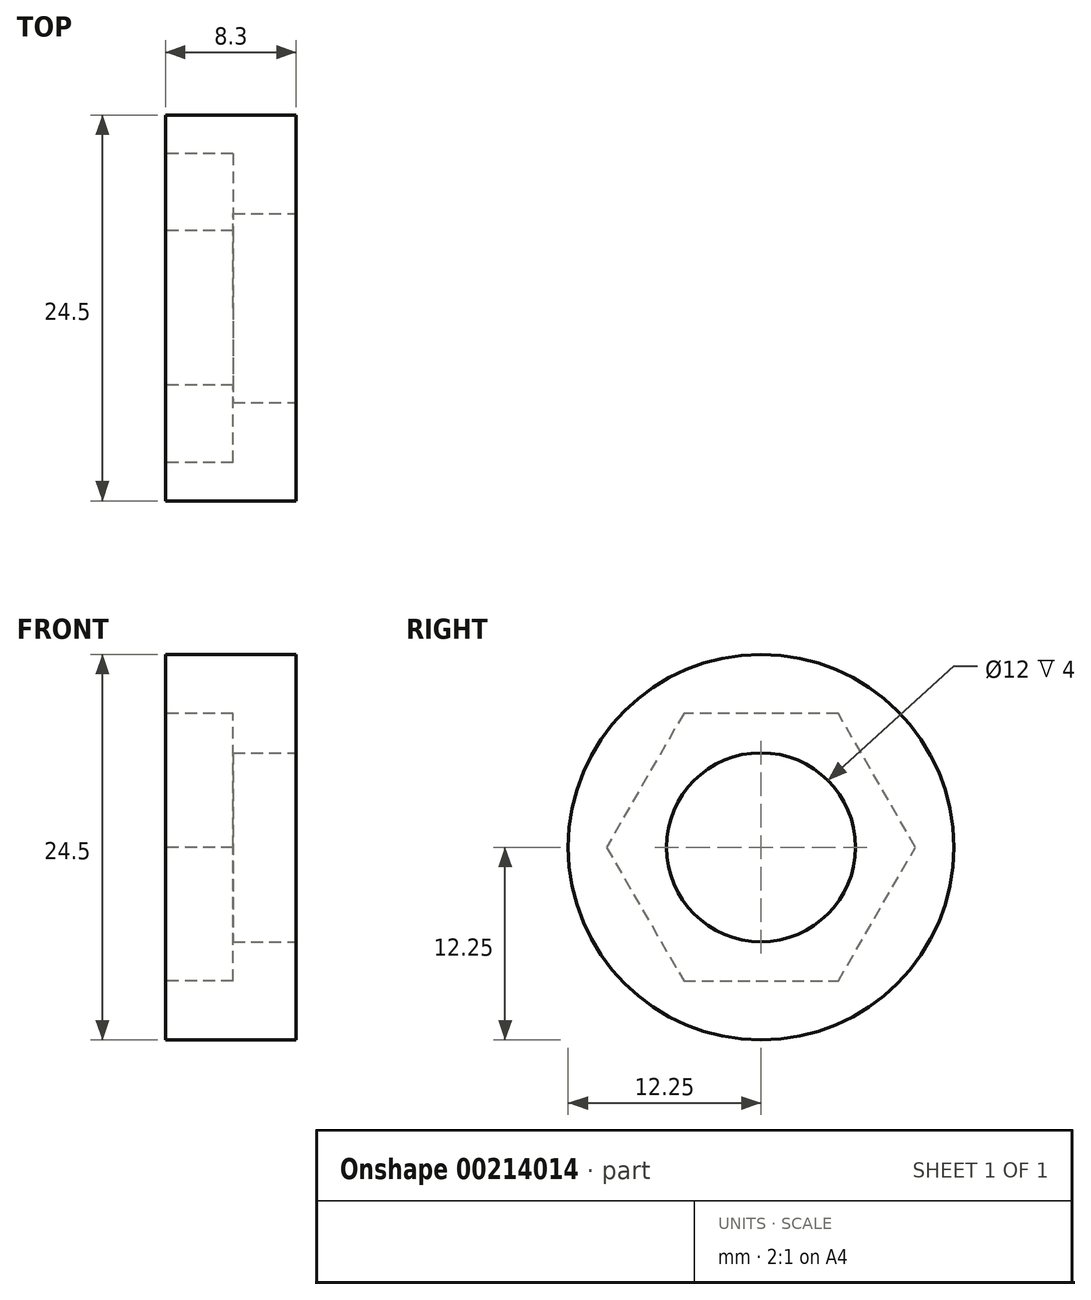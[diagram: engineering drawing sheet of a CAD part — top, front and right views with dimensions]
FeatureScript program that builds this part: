
annotation { "Feature Type Name" : "Feature", "Feature Type Description" : "" }
export const myFeature = defineFeature(function(context is Context, id is Id, definition is map)
    precondition{}
    {
        {
            var Q0;
            Q0=qCreatedBy(makeId("Right.planeOp"),FACE);
            var sketch = newSketch(context, id + "F0", { "sketchPlane" : qUnion([Q0])});
            skCircle(sketch, "E0", {"center": v(0, 0) * mm, "radius": 12.25 * mm});
            skSolve(sketch);
        }
        {
            var Q0;
            Q0 = qSketchRegion(id + "F0", true);
            extrude(context, id + "F1", {"entities" : qUnion([Q0]), "depth" : 8.3 * mm});
        }
        {
            var Q0;
            Q0=makeQuery(id+"F1.opExtrude","CAP_FACE",FACE,{"disambiguationData":[OSD([sQuery(id+"F0.wireOp",EDGE,"E0")])],"isStart":false});
            var sketch = newSketch(context, id + "F2", { "sketchPlane" : qUnion([Q0])});
            skCircle(sketch, "E1", {"center": v(0, 0) * mm, "radius": 6 * mm});
            skSolve(sketch);
        }
        {
            var Q0;
            Q0 = qSketchRegion(id + "F2", true);
            extrude(context, id + "F3", {"entities" : qUnion([Q0]), "operationType" : NewBodyOperationType.REMOVE, "endBound" : BoundingType.THROUGH_ALL, "oppositeDirection" : true, "depth" : 25.4 * mm});
        }
        {
            var Q0;
            Q0=makeQuery(id+"F1.opExtrude","CAP_FACE",FACE,{"disambiguationData":[OSD([sQuery(id+"F0.wireOp",EDGE,"E0")])],"isStart":true});
            var sketch = newSketch(context, id + "F4", { "sketchPlane" : qUnion([Q0])});
            skCircle(sketch, "E2.cCircle", {"center": v(0, 0) * mm, "radius": 8.5 * mm, "construction": true});
            skLineSegment(sketch, "E2.0", {"start": v(-4.9, 8.5) * mm, "end": v(4.9, 8.5) * mm});
            skLineSegment(sketch, "E2.1", {"start": v(4.9, 8.5) * mm, "end": v(9.81, 0) * mm});
            skLineSegment(sketch, "E2.2", {"start": v(9.81, 0) * mm, "end": v(4.9, -8.5) * mm});
            skLineSegment(sketch, "E2.3", {"start": v(4.9, -8.5) * mm, "end": v(-4.9, -8.5) * mm});
            skLineSegment(sketch, "E2.4", {"start": v(-4.9, -8.5) * mm, "end": v(-9.81, 0) * mm});
            skLineSegment(sketch, "E2.5", {"start": v(-9.81, 0) * mm, "end": v(-4.9, 8.5) * mm});
            skPoint(sketch, "E2.0.midPoint", {"position": v(0, 8.5) * mm});
            skSolve(sketch);
        }
        {
            var Q0;
            Q0 = qSketchRegion(id + "F4", true);
            extrude(context, id + "F5", {"entities" : qUnion([Q0]), "operationType" : NewBodyOperationType.REMOVE, "oppositeDirection" : true, "depth" : 4.3 * mm});
        }
    });
